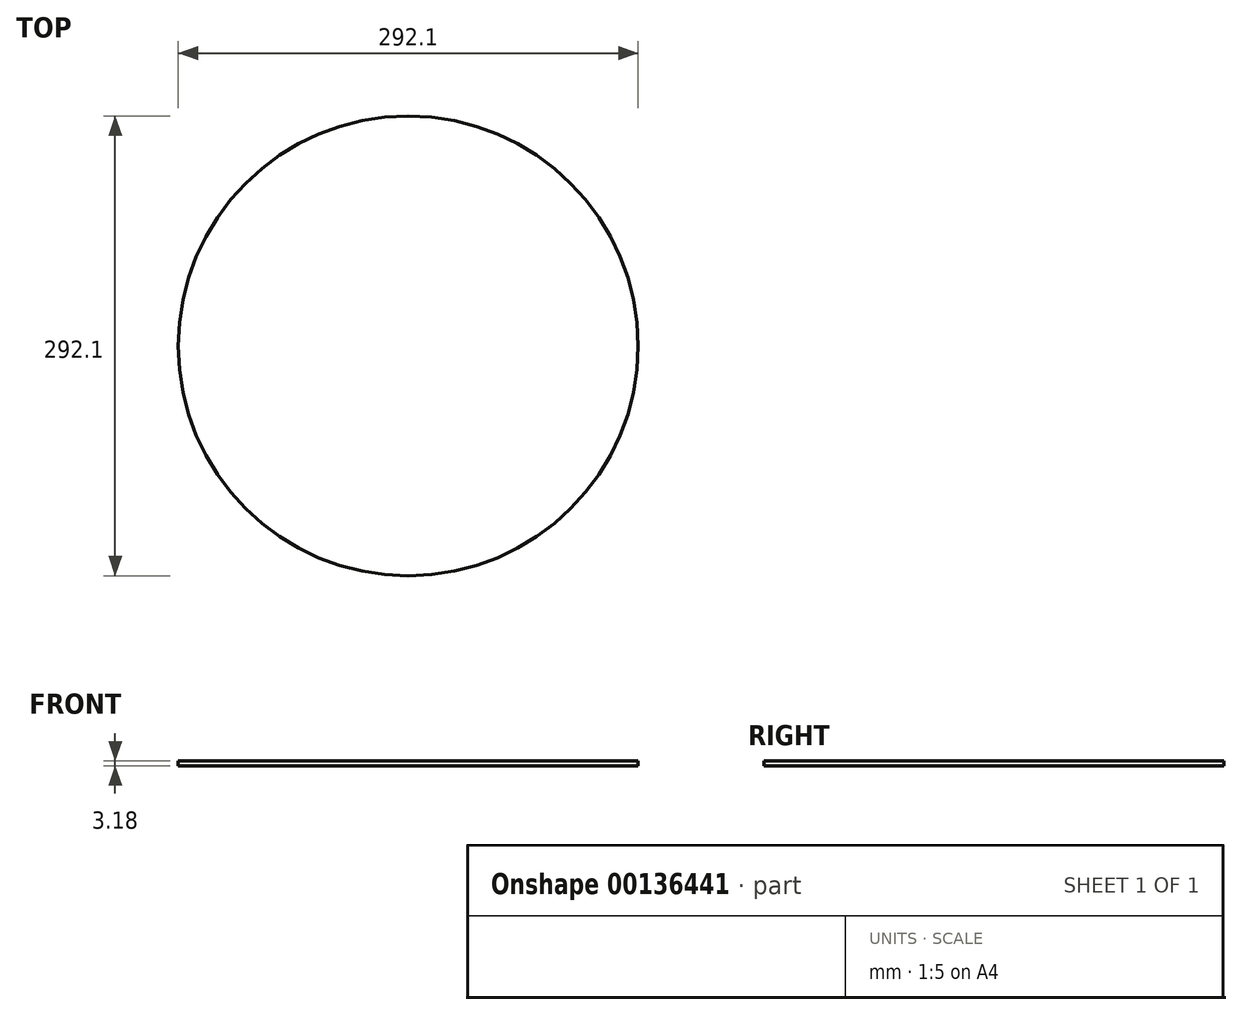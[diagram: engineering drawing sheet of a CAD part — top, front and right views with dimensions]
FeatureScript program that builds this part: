
annotation { "Feature Type Name" : "Feature", "Feature Type Description" : "" }
export const myFeature = defineFeature(function(context is Context, id is Id, definition is map)
    precondition{}
    {
        {
            var Q0;
            Q0=qCreatedBy(makeId("Top.planeOp"),FACE);
            var sketch = newSketch(context, id + "F0", { "sketchPlane" : qUnion([Q0])});
            skCircle(sketch, "E0", {"center": v(0, 0) * mm, "radius": 146.05 * mm});
            skSolve(sketch);
        }
        {
            var Q0;
            Q0=makeQuery(id+"F0.imprint","IMPRINT",FACE,{"disambiguationData":[TD([[makeQuery(id+"F0.imprint","IMPRINT",EDGE,{"derivedFrom":sQuery(id+"F0.wireOp",EDGE,"E0")}),1.0]])]});
            extrude(context, id + "F1", {"entities" : qUnion([Q0]), "depth" : 3.17 * mm});
        }
    });
